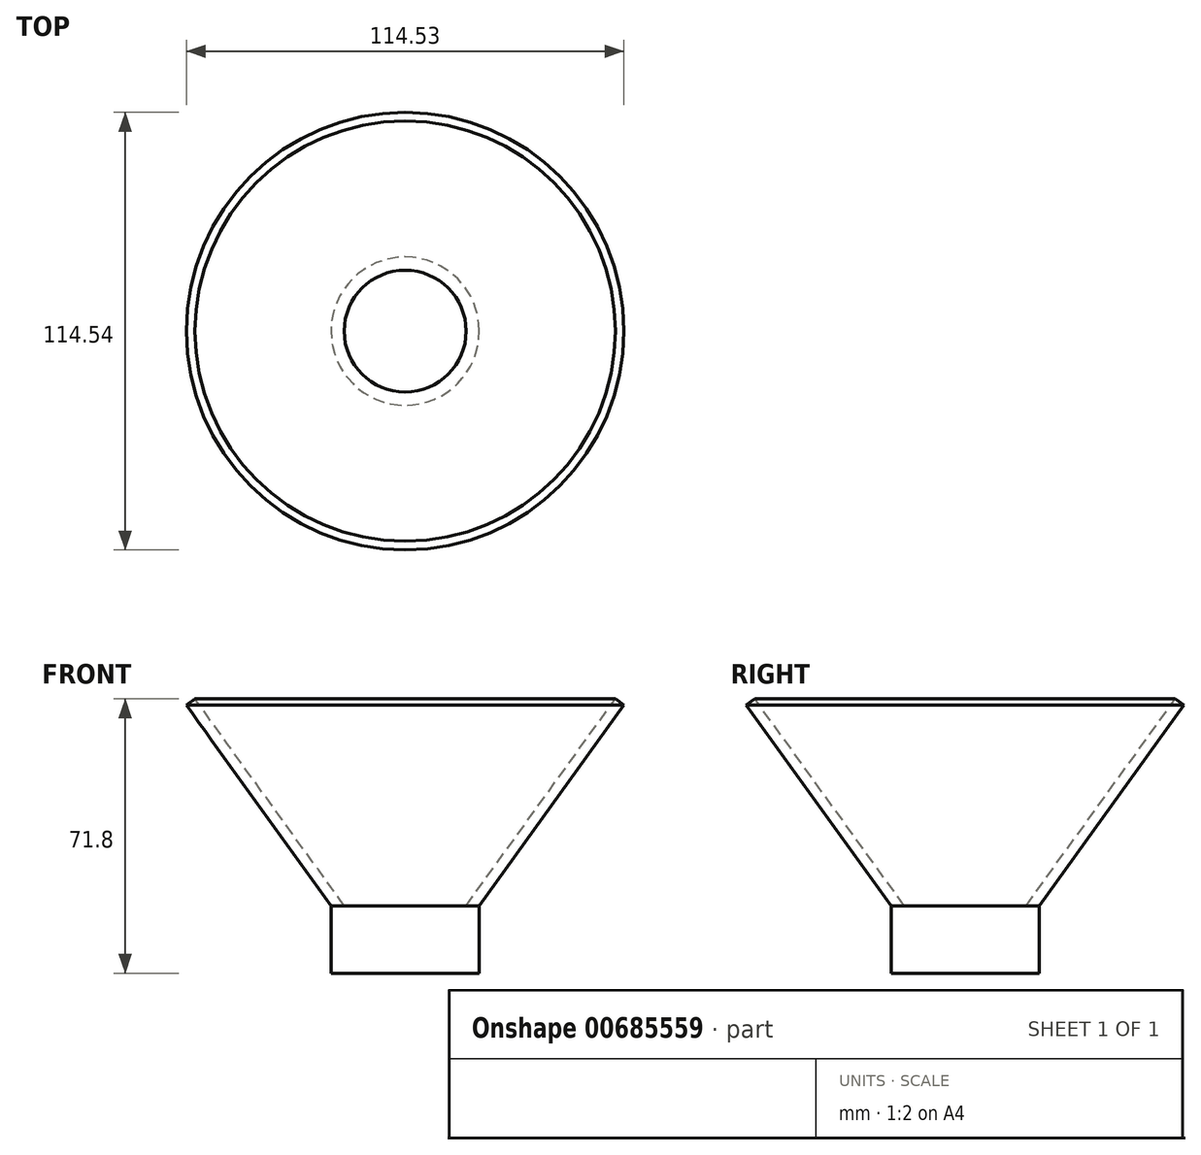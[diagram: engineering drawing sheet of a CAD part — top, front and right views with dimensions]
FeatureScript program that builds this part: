
annotation { "Feature Type Name" : "Feature", "Feature Type Description" : "" }
export const myFeature = defineFeature(function(context is Context, id is Id, definition is map)
    precondition{}
    {
        {
            var Q0;
            Q0=qCreatedBy(makeId("Front.planeOp"),FACE);
            var sketch = newSketch(context, id + "F0", { "sketchPlane" : qUnion([Q0])});
            skLineSegment(sketch, "E0", {"start": v(0, 0) * mm, "end": v(39.05, 54.14) * mm});
            skLineSegment(sketch, "E1", {"start": v(39.05, 54.14) * mm, "end": v(41.32, 52.5) * mm});
            skLineSegment(sketch, "E2", {"start": v(41.32, 52.5) * mm, "end": v(3.46, 0) * mm});
            skLineSegment(sketch, "E3", {"start": v(3.46, 0) * mm, "end": v(3.46, -17.66) * mm});
            skLineSegment(sketch, "E4", {"start": v(3.46, -17.66) * mm, "end": v(-15.94, -17.66) * mm});
            skLineSegment(sketch, "E5", {"start": v(-15.94, -17.66) * mm, "end": v(-15.94, 0) * mm});
            skLineSegment(sketch, "E6", {"start": v(-15.94, 0) * mm, "end": v(0, 0) * mm});
            skSolve(sketch);
        }
        {
            var Q0;
            Q0 = qSketchRegion(id + "F0", true);
            var Q1;
            Q1=sQuery(id+"F0.wireOp",EDGE,"E5");
            revolve(context, id + "F1", {"surfaceOperationType" : NewSurfaceOperationType.NEW, "entities" : qUnion([Q0]), "axis" : qUnion([Q1]), "revolveType" : RevolveType.FULL});
        }
    });
